# Revit family: Interceptor_Solids-Zurn-Z1183-FC
name_source: partatom
category: Plumbing Fixtures
units: mm (PartAtom-declared; Revit-internal decimal feet)

## family parameters
Always vertical = Yes
Cut with Voids When Loaded = No
Maintain Annotation Orientation = No
OmniClass Number = 23.45.30.00
OmniClass Title = Washing and Waste Disposal Equipment
Part Type = Normal
Room Calculation Point = No
Round Connector Dimension = Use Radius
Shared = No
Work Plane-Based = No

## types (24) — shared parameters
Assembly Code = D2090300
CW Connection = No
Default Elevation = 20 "
Description = SOLIDS INTERCEPTOR W/ FLUSH COVER
HW Connection = No
Manufacturer = Zurn Water, LLC
Manufacurer Brand = Zurn
Modified Date = 02/20/26
Product Documentation Link = https://files.zurn.com
Product Page URL = https://www.zurn.com
Product data url = https://www.bimobject.com
URL = www.zurn.com
Vent Connection = No
Waste Connection = Yes
zero-valued in all types: CWFU, HWFU, WFU

## per-type parameters (varying)
| type | Dim C | Dim D/ E | Dim G | Flow Rate (GPM) | Handle height | Main Material | Model | Pipe Size 'A' (Inner Diameter) | Pipe Size 'A' (Inner Radius) | Pipe Size 'A' (Nominal Diameter) | Pipe Size 'A' (Nominal Radius) | Pipe Size 'A' (Outer Diameter) | Pipe Size 'A' (Outer Radius) | Solids Capacity | Type Comments |
| Z1183-FC-1000-100-3 | 27 " | 23 " | 24.375 " | 100 GPM | 4.437 " | Steel - Zurn - A.R.E Coated | Z1183-FC | 3.068 " | 1.534 " | 3 " | 1.5 " | 3.5 " | 1.75 " | 1.80 ft³ | Z1183-FC-1000-100 GPM with 3 Inch Inlet/ outlet |
| Z1183-FC-100-4-2 | 10 " | 7.25 " | 11.75 " | 4 GPM | 3.437 " | Steel - Zurn - A.R.E Coated | Z1183-FC | 2.067 " | 1.034 " | 2 " | 1 " | 2.375 " | 1.188 " | 0.20 ft³ | Z1183-FC-100-4 GPM with 2 Inch Inlet/ outlet |
| Z1183-FC-1100-125-3 | 30.125 " | 24.5 " | 24.375 " | 125 GPM | 4.437 " | Steel - Zurn - A.R.E Coated | Z1183-FC | 3.068 " | 1.534 " | 3 " | 1.5 " | 3.5 " | 1.75 " | 1.95 ft³ | Z1183-FC-1100-125 GPM with 3 Inch Inlet/ outlet |
| Z1183-FC-1200-150-4 | 30.75 " | 25.25 " | 24.375 " | 150 GPM | 4.437 " | Steel - Zurn - A.R.E Coated | Z1183-FC | 4.026 " | 2.013 " | 4 " | 2 " | 4.5 " | 2.25 " | 2.11 ft³ | Z1183-FC-1200-150 GPM with 4 Inch Inlet/ outlet |
| Z1183-FC-200-7-2 | 11.125 " | 8.125 " | 13.75 " | 7 GPM | 3.437 " | Steel - Zurn - A.R.E Coated | Z1183-FC | 2.067 " | 1.034 " | 2 " | 1 " | 2.375 " | 1.188 " | 0.29 ft³ | Z1183-FC-200-7 GPM with 2 Inch Inlet/ outlet |
| Z1183-FC-300-10-3 | 11.75 " | 8.25 " | 15.875 " | 10 GPM | 3.437 " | Steel - Zurn - A.R.E Coated | Z1183-FC | 3.068 " | 1.534 " | 3 " | 1.5 " | 3.5 " | 1.75 " | 0.33 ft³ | Z1183-FC-300-10 GPM with 3 Inch Inlet/ outlet |
| Z1183-FC-400-15-3 | 13.375 " | 9.375 " | 16.75 " | 15 GPM | 3.437 " | Steel - Zurn - A.R.E Coated | Z1183-FC | 3.068 " | 1.534 " | 3 " | 1.5 " | 3.5 " | 1.75 " | 0.38 ft³ | Z1183-FC-400-15 GPM with 3 Inch Inlet/ outlet |
| Z1183-FC-500-20-3 | 15 " | 11.75 " | 19.125 " | 20 GPM | 3.437 " | Steel - Zurn - A.R.E Coated | Z1183-FC | 3.068 " | 1.534 " | 3 " | 1.5 " | 3.5 " | 1.75 " | 0.66 ft³ | Z1183-FC-500-20 GPM with 3 Inch Inlet/ outlet |
| Z1183-FC-600-25-3 | 17 " | 12.438 " | 21.75 " | 25 GPM | 4.437 " | Steel - Zurn - A.R.E Coated | Z1183-FC | 3.068 " | 1.534 " | 3 " | 1.5 " | 3.5 " | 1.75 " | 0.79 ft³ | Z1183-FC-600-25 GPM with 3 Inch Inlet/ outlet |
| Z1183-FC-700-35-3 | 18.75 " | 14.188 " | 24.375 " | 35 GPM | 4.437 " | Steel - Zurn - A.R.E Coated | Z1183-FC | 3.068 " | 1.534 " | 3 " | 1.5 " | 3.5 " | 1.75 " | 1.17 ft³ | Z1183-FC-700-35 GPM with 3 Inch Inlet/ outlet |
| Z1183-FC-800-50-3 | 21.125 " | 16 " | 24.375 " | 50 GPM | 4.437 " | Steel - Zurn - A.R.E Coated | Z1183-FC | 3.068 " | 1.534 " | 3 " | 1.5 " | 3.5 " | 1.75 " | 1.35 ft³ | Z1183-FC-800-50 GPM with 3 Inch Inlet/ outlet |
| Z1183-FC-900-75-3 | 22.75 " | 18.5 " | 24.375 " | 75 GPM | 4.437 " | Steel - Zurn - A.R.E Coated | Z1183-FC | 3.068 " | 1.534 " | 3 " | 1.5 " | 3.5 " | 1.75 " | 1.61 ft³ | Z1183-FC-900-75 GPM with 3 Inch Inlet/ outlet |
| ZS1183-FC-1000-100-3 | 27 " | 23 " | 24.375 " | 100 GPM | 4.437 " | Steel - Zurn - Stainless - Type - 304 | ZS1183-FC | 3.068 " | 1.534 " | 3 " | 1.5 " | 3.5 " | 1.75 " | 1.80 ft³ | ZS1183-FC-1000-100 GPM with 3 Inch Inlet/ outlet |
| ZS1183-FC-100-4-2 | 10 " | 7.25 " | 11.75 " | 4 GPM | 3.437 " | Steel - Zurn - Stainless - Type - 304 | ZS1183-FC | 2.067 " | 1.034 " | 2 " | 1 " | 2.375 " | 1.188 " | 0.20 ft³ | ZS1183-FC-100-4 GPM with 2 Inch Inlet/ outlet |
| ZS1183-FC-1100-125-3 | 30.125 " | 24.5 " | 24.375 " | 125 GPM | 4.437 " | Steel - Zurn - Stainless - Type - 304 | ZS1183-FC | 3.068 " | 1.534 " | 3 " | 1.5 " | 3.5 " | 1.75 " | 1.80 ft³ | ZS1183-FC-1100-125 GPM with 3 Inch Inlet/ outlet |
| ZS1183-FC-1200-150-4 | 30.75 " | 25.25 " | 24.375 " | 150 GPM | 4.437 " | Steel - Zurn - Stainless - Type - 304 | ZS1183-FC | 3.068 " | 1.534 " | 4 " | 2 " | 4.5 " | 2.25 " | 1.80 ft³ | ZS1183-FC-1200-150 GPM with 4 Inch Inlet/ outlet |
| ZS1183-FC-200-7-2 | 11.125 " | 8.125 " | 13.75 " | 7 GPM | 3.437 " | Steel - Zurn - Stainless - Type - 304 | ZS1183-FC | 2.067 " | 1.034 " | 2 " | 1 " | 2.375 " | 1.188 " | 0.29 ft³ | ZS1183-FC-200-7 GPM with 2 Inch Inlet/ outlet |
| ZS1183-FC-300-10-3 | 11.75 " | 8.25 " | 15.875 " | 10 GPM | 3.437 " | Steel - Zurn - Stainless - Type - 304 | ZS1183-FC | 3.068 " | 1.534 " | 3 " | 1.5 " | 3.5 " | 1.75 " | 0.33 ft³ | ZS1183-FC-300-10 GPM with 3 Inch Inlet/ outlet |
| ZS1183-FC-400-15-3 | 13.375 " | 9.375 " | 16.75 " | 15 GPM | 3.437 " | Steel - Zurn - Stainless - Type - 304 | ZS1183-FC | 3.068 " | 1.534 " | 3 " | 1.5 " | 3.5 " | 1.75 " | 0.38 ft³ | ZS1183-FC-400-15 GPM with 3 Inch Inlet/ outlet |
| ZS1183-FC-500-20-3 | 15 " | 11.75 " | 19.125 " | 20 GPM | 3.437 " | Steel - Zurn - Stainless - Type - 304 | ZS1183-FC | 3.068 " | 1.534 " | 3 " | 1.5 " | 3.5 " | 1.75 " | 0.66 ft³ | ZS1183-FC-500-20 GPM with 3 Inch Inlet/ outlet |
| ZS1183-FC-600-25-3 | 17 " | 12.438 " | 21.75 " | 25 GPM | 4.437 " | Steel - Zurn - Stainless - Type - 304 | ZS1183-FC | 3.068 " | 1.534 " | 3 " | 1.5 " | 3.5 " | 1.75 " | 0.79 ft³ | ZS1183-FC-600-25 GPM with 3 Inch Inlet/ outlet |
| ZS1183-FC-700-35-3 | 18.75 " | 14.188 " | 24.375 " | 35 GPM | 4.437 " | Steel - Zurn - Stainless - Type - 304 | ZS1183-FC | 3.068 " | 1.534 " | 3 " | 1.5 " | 3.5 " | 1.75 " | 1.17 ft³ | ZS1183-FC-700-35 GPM with 3 Inch Inlet/ outlet |
| ZS1183-FC-800-50-3 | 21.125 " | 16 " | 24.375 " | 50 GPM | 4.437 " | Steel - Zurn - Stainless - Type - 304 | ZS1183-FC | 3.068 " | 1.534 " | 3 " | 1.5 " | 3.5 " | 1.75 " | 1.35 ft³ | ZS1183-FC-800-50 GPM with 3 Inch Inlet/ outlet |
| ZS1183-FC-900-75-3 | 22.75 " | 18.5 " | 24.375 " | 75 GPM | 4.437 " | Steel - Zurn - Stainless - Type - 304 | ZS1183-FC | 3.068 " | 1.534 " | 3 " | 1.5 " | 3.5 " | 1.75 " | 1.61 ft³ | ZS1183-FC-900-75 GPM with 3 Inch Inlet/ outlet |

## geometry (parser evidence)
native form markers: Sweep x2
no freeform markers — native parametric forms only
